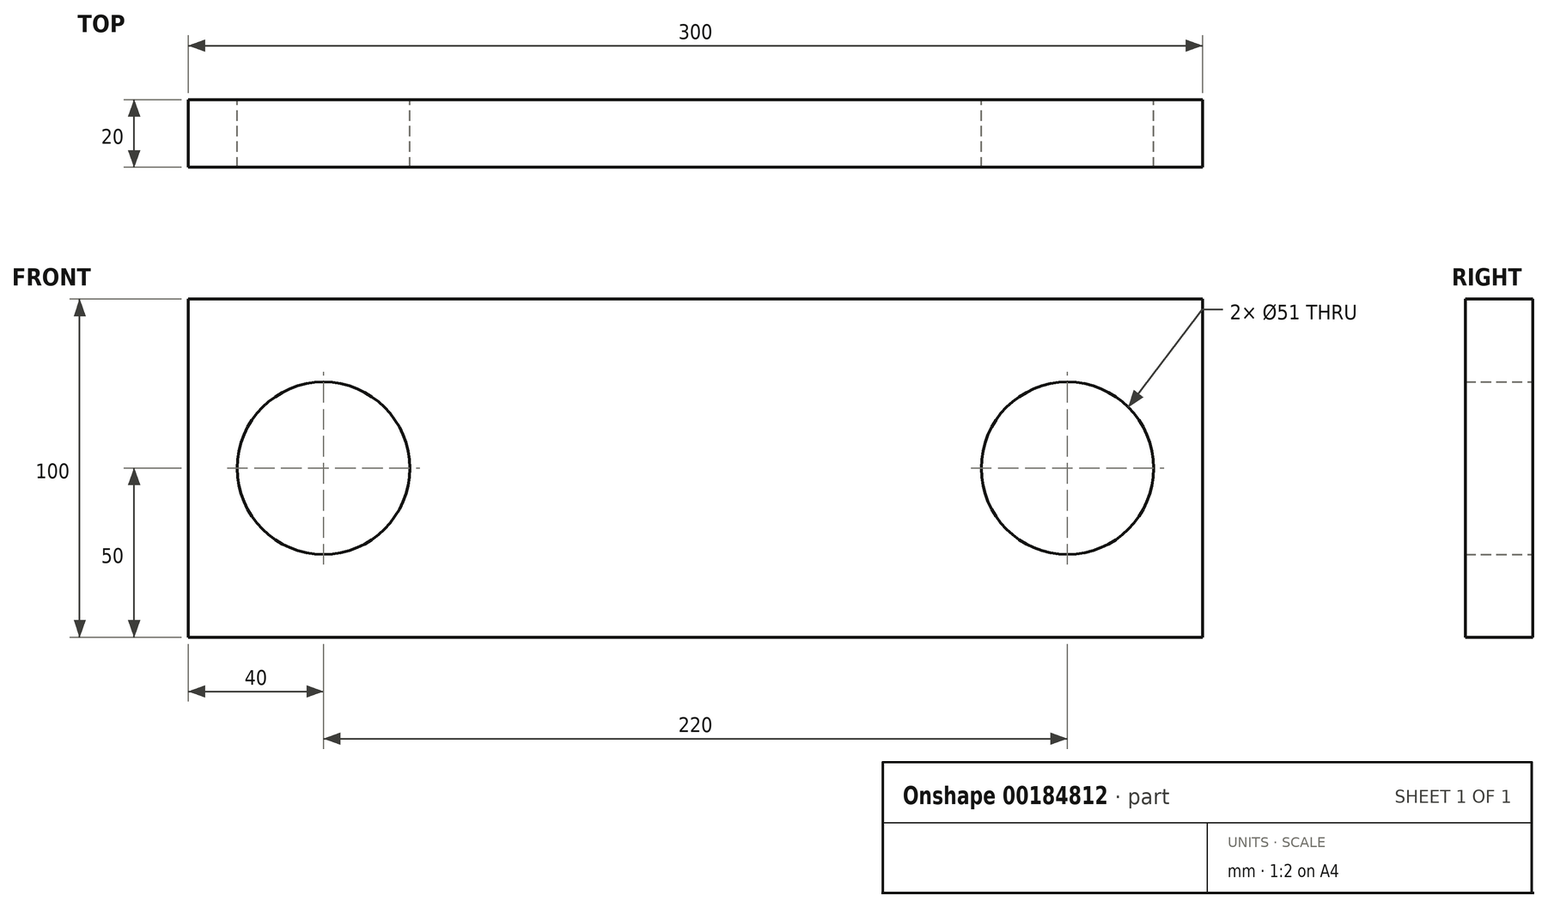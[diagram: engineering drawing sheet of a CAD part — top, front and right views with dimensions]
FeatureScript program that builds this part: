
annotation { "Feature Type Name" : "Feature", "Feature Type Description" : "" }
export const myFeature = defineFeature(function(context is Context, id is Id, definition is map)
    precondition{}
    {
        {
            var Q0;
            Q0=qCreatedBy(makeId("Front.planeOp"),FACE);
            var sketch = newSketch(context, id + "F0", { "sketchPlane" : qUnion([Q0])});
            skLineSegment(sketch, "E0.bottom", {"start": v(0, 0) * mm, "end": v(300, 0) * mm});
            skLineSegment(sketch, "E0.top", {"start": v(0, 100) * mm, "end": v(300, 100) * mm});
            skLineSegment(sketch, "E0.left", {"start": v(0, 0) * mm, "end": v(0, 100) * mm});
            skLineSegment(sketch, "E0.right", {"start": v(300, 0) * mm, "end": v(300, 100) * mm});
            skLineSegment(sketch, "E1", {"start": v(0, 50) * mm, "end": v(40, 50) * mm, "construction": true});
            skCircle(sketch, "E2", {"center": v(40, 50) * mm, "radius": 25.5 * mm});
            skLineSegment(sketch, "E3", {"start": v(300, 50) * mm, "end": v(260, 50) * mm, "construction": true});
            skCircle(sketch, "E4", {"center": v(260, 50) * mm, "radius": 25.5 * mm});
            skSolve(sketch);
        }
        {
            var Q0;
            Q0=makeQuery(id+"F0.imprint","IMPRINT",FACE,{"disambiguationData":[TD([[makeQuery(id+"F0.imprint","IMPRINT",EDGE,{"derivedFrom":sQuery(id+"F0.wireOp",EDGE,"E0.bottom")}),1.0]])]});
            extrude(context, id + "F1", {"entities" : qUnion([Q0]), "depth" : 20 * mm});
        }
    });
